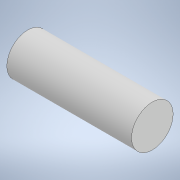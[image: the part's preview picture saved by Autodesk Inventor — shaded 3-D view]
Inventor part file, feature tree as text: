
AUTODESK INVENTOR PART (.ipt)
format: ipt  version: 2022.2 (Build 262287030, 287C)  size: 107,520 bytes
history: native  units: in
note: dims shown in document units (in); Inventor stores cm internally (conversion verified against a paired STEP export)
features: extrude x1
ambient origin geometry x8: Origin, YZ Plane, XZ Plane, XY Plane, X Axis, Y Axis, Z Axis, Center Point
bodies: Solid1 (feature_tree)
feature tree (1):
  extrude  "Extrude1"  [1 undecoded]
note: 1 required parameter value undecoded (feature->parameter linkage not recoverable at this tier; creation-order binding heuristic only, values carry confidence <= 0.55)
